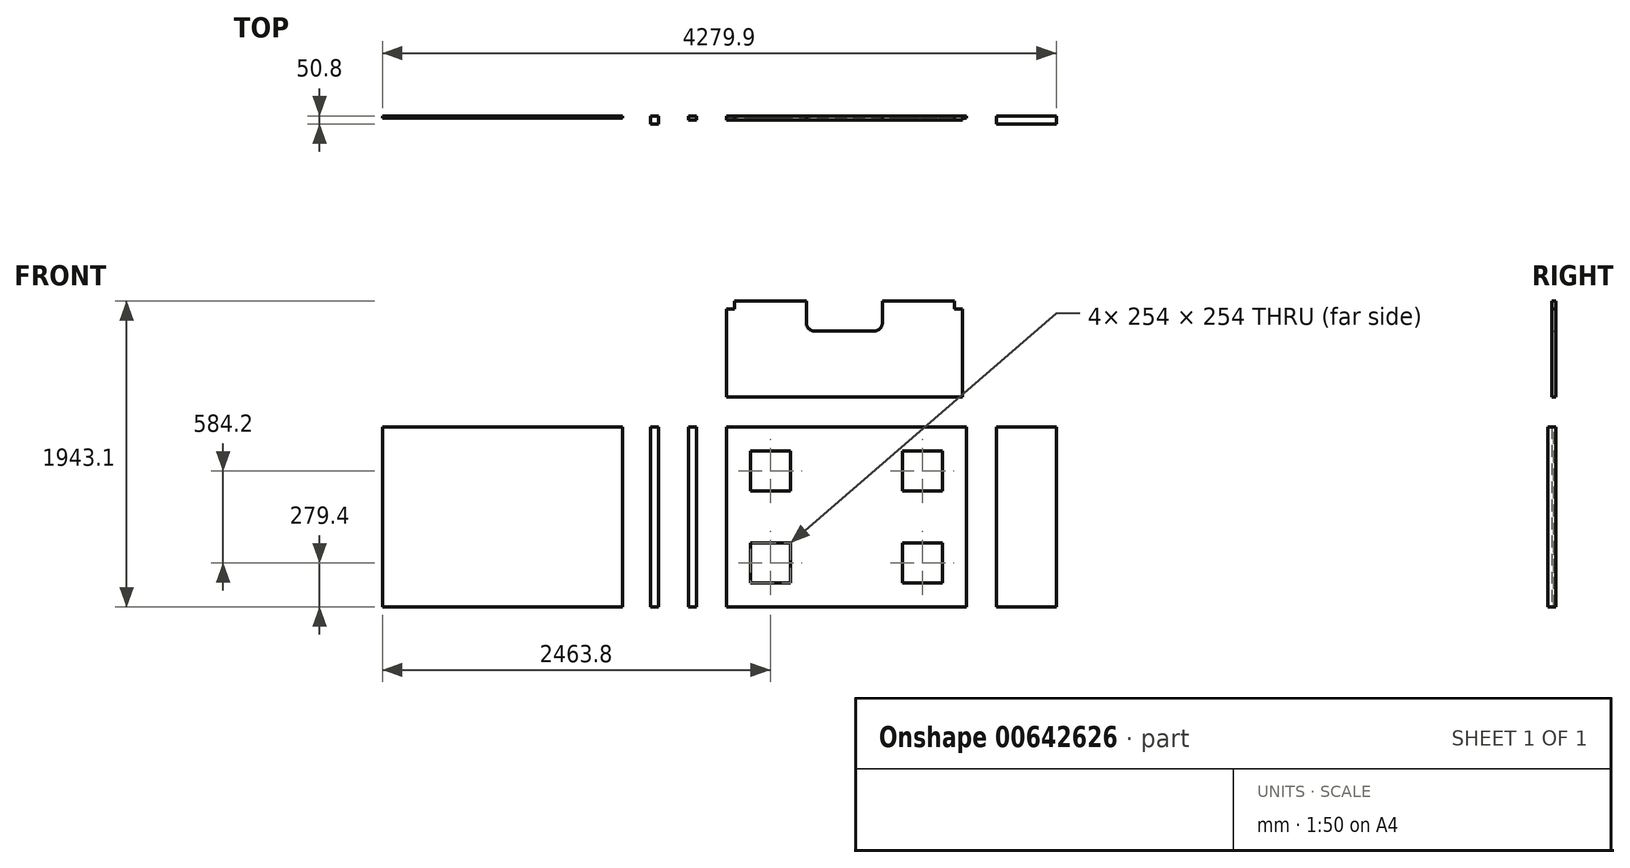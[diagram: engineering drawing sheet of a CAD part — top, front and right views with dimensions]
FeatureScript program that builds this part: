
annotation { "Feature Type Name" : "Feature", "Feature Type Description" : "" }
export const myFeature = defineFeature(function(context is Context, id is Id, definition is map)
    precondition{}
    {
        {
            var Q0;
            Q0=qCreatedBy(makeId("Front.planeOp"),FACE);
            var sketch = newSketch(context, id + "F0", { "sketchPlane" : qUnion([Q0])});
            skLineSegment(sketch, "E0.bottom", {"start": v(0, 1143) * mm, "end": v(50.8, 1143) * mm});
            skLineSegment(sketch, "E0.top", {"start": v(0, 0) * mm, "end": v(50.8, 0) * mm});
            skLineSegment(sketch, "E0.left", {"start": v(0, 1143) * mm, "end": v(0, 0) * mm});
            skLineSegment(sketch, "E0.right", {"start": v(50.8, 1143) * mm, "end": v(50.8, 0) * mm});
            skSolve(sketch);
        }
        {
            var Q0;
            Q0 = qSketchRegion(id + "F0", true);
            extrude(context, id + "F1", {"entities" : qUnion([Q0]), "depth" : 50.8 * mm, "offsetDistance" : 25.4 * mm});
        }
        {
            var Q0;
            Q0=qCreatedBy(makeId("Front.planeOp"),FACE);
            var sketch = newSketch(context, id + "F2", { "sketchPlane" : qUnion([Q0])});
            skLineSegment(sketch, "E1.bottom", {"start": v(241.3, 1143) * mm, "end": v(292.1, 1143) * mm});
            skLineSegment(sketch, "E1.top", {"start": v(241.3, 0) * mm, "end": v(292.1, 0) * mm});
            skLineSegment(sketch, "E1.left", {"start": v(241.3, 1143) * mm, "end": v(241.3, 0) * mm});
            skLineSegment(sketch, "E1.right", {"start": v(292.1, 1143) * mm, "end": v(292.1, 0) * mm});
            skSolve(sketch);
        }
        {
            var Q0;
            Q0 = qSketchRegion(id + "F2", true);
            extrude(context, id + "F3", {"entities" : qUnion([Q0]), "depth" : 25.4 * mm, "offsetDistance" : 25.4 * mm});
        }
        {
            var Q0;
            Q0=qCreatedBy(makeId("Front.planeOp"),FACE);
            var sketch = newSketch(context, id + "F4", { "sketchPlane" : qUnion([Q0])});
            skLineSegment(sketch, "E2.bottom", {"start": v(-177.8, 0) * mm, "end": v(-1701.8, 0) * mm});
            skLineSegment(sketch, "E2.top", {"start": v(-177.8, 1143) * mm, "end": v(-1701.8, 1143) * mm});
            skLineSegment(sketch, "E2.left", {"start": v(-177.8, 0) * mm, "end": v(-177.8, 1143) * mm});
            skLineSegment(sketch, "E2.right", {"start": v(-1701.8, 0) * mm, "end": v(-1701.8, 1143) * mm});
            skSolve(sketch);
        }
        {
            var Q0;
            Q0 = qSketchRegion(id + "F4", true);
            extrude(context, id + "F5", {"entities" : qUnion([Q0]), "depth" : 12.7 * mm, "offsetDistance" : 25.4 * mm});
        }
        {
            var Q0;
            Q0=qCreatedBy(makeId("Front.planeOp"),FACE);
            var sketch = newSketch(context, id + "F6", { "sketchPlane" : qUnion([Q0])});
            skLineSegment(sketch, "E3.bottom", {"start": v(482.6, 1143) * mm, "end": v(2006.6, 1143) * mm});
            skLineSegment(sketch, "E3.top", {"start": v(482.6, 0) * mm, "end": v(2006.6, 0) * mm});
            skLineSegment(sketch, "E3.left", {"start": v(482.6, 1143) * mm, "end": v(482.6, 0) * mm});
            skLineSegment(sketch, "E3.right", {"start": v(2006.6, 1143) * mm, "end": v(2006.6, 0) * mm});
            skLineSegment(sketch, "E4.bottom", {"start": v(635, 990.6) * mm, "end": v(889, 990.6) * mm});
            skLineSegment(sketch, "E4.top", {"start": v(635, 736.6) * mm, "end": v(889, 736.6) * mm});
            skLineSegment(sketch, "E4.left", {"start": v(635, 990.6) * mm, "end": v(635, 736.6) * mm});
            skLineSegment(sketch, "E4.right", {"start": v(889, 990.6) * mm, "end": v(889, 736.6) * mm});
            skLineSegment(sketch, "E5.bottom", {"start": v(635, 406.4) * mm, "end": v(889, 406.4) * mm});
            skLineSegment(sketch, "E5.top", {"start": v(635, 152.4) * mm, "end": v(889, 152.4) * mm});
            skLineSegment(sketch, "E5.left", {"start": v(635, 406.4) * mm, "end": v(635, 152.4) * mm});
            skLineSegment(sketch, "E5.right", {"start": v(889, 406.4) * mm, "end": v(889, 152.4) * mm});
            skLineSegment(sketch, "E6.bottom", {"start": v(1600.2, 990.6) * mm, "end": v(1854.2, 990.6) * mm});
            skLineSegment(sketch, "E6.top", {"start": v(1600.2, 736.6) * mm, "end": v(1854.2, 736.6) * mm});
            skLineSegment(sketch, "E6.left", {"start": v(1600.2, 990.6) * mm, "end": v(1600.2, 736.6) * mm});
            skLineSegment(sketch, "E6.right", {"start": v(1854.2, 990.6) * mm, "end": v(1854.2, 736.6) * mm});
            skLineSegment(sketch, "E7.bottom", {"start": v(1854.2, 406.4) * mm, "end": v(1600.2, 406.4) * mm});
            skLineSegment(sketch, "E7.top", {"start": v(1854.2, 152.4) * mm, "end": v(1600.2, 152.4) * mm});
            skLineSegment(sketch, "E7.left", {"start": v(1854.2, 406.4) * mm, "end": v(1854.2, 152.4) * mm});
            skLineSegment(sketch, "E7.right", {"start": v(1600.2, 406.4) * mm, "end": v(1600.2, 152.4) * mm});
            skLineSegment(sketch, "E8", {"start": v(1244.6, 1143) * mm, "end": v(1244.6, 0) * mm, "construction": true});
            skLineSegment(sketch, "E9", {"start": v(482.6, 571.5) * mm, "end": v(2006.6, 571.5) * mm, "construction": true});
            skSolve(sketch);
        }
        {
            var Q0;
            Q0 = qSketchRegion(id + "F6", true);
            extrude(context, id + "F7", {"entities" : qUnion([Q0]), "depth" : 12.7 * mm, "offsetDistance" : 25.4 * mm});
        }
        {
            var Q0;
            Q0=qCreatedBy(makeId("Front.planeOp"),FACE);
            var sketch = newSketch(context, id + "F8", { "sketchPlane" : qUnion([Q0])});
            skLineSegment(sketch, "E10.bottom", {"start": v(482.6, 1333.5) * mm, "end": v(1981.2, 1333.5) * mm});
            skLineSegment(sketch, "E11.top", {"start": v(1041.4, 1752.6) * mm, "end": v(1422.4, 1752.6) * mm});
            skLineSegment(sketch, "E11.left", {"start": v(990.6, 1943.1) * mm, "end": v(990.6, 1803.4) * mm});
            skLineSegment(sketch, "E11.right", {"start": v(1473.2, 1943.1) * mm, "end": v(1473.2, 1803.4) * mm});
            skPoint(sketch, "E12.visualSharp", {"position": v(990.6, 1752.6) * mm});
            skArc(sketch, "E12.filletArc", {"start": v(990.6, 1803.4) * mm, "mid": v(1005.48, 1767.48) * mm, "end": v(1041.4, 1752.6) * mm});
            skPoint(sketch, "E13.visualSharp", {"position": v(1473.2, 1752.6) * mm});
            skArc(sketch, "E13.filletArc", {"start": v(1422.4, 1752.6) * mm, "mid": v(1458.32, 1767.48) * mm, "end": v(1473.2, 1803.4) * mm});
            skLineSegment(sketch, "E14", {"start": v(482.6, 1892.3) * mm, "end": v(533.4, 1892.3) * mm});
            skLineSegment(sketch, "E15", {"start": v(533.4, 1892.3) * mm, "end": v(533.4, 1943.1) * mm});
            skLineSegment(sketch, "E16", {"start": v(1930.4, 1943.1) * mm, "end": v(1930.4, 1892.3) * mm});
            skLineSegment(sketch, "E17", {"start": v(1930.4, 1892.3) * mm, "end": v(1981.2, 1892.3) * mm});
            skLineSegment(sketch, "E18", {"start": v(533.4, 1943.1) * mm, "end": v(990.6, 1943.1) * mm});
            skLineSegment(sketch, "E19", {"start": v(1473.2, 1943.1) * mm, "end": v(1930.4, 1943.1) * mm});
            skLineSegment(sketch, "E20", {"start": v(482.6, 1892.3) * mm, "end": v(482.6, 1333.5) * mm});
            skLineSegment(sketch, "E21", {"start": v(1981.2, 1333.5) * mm, "end": v(1981.2, 1892.3) * mm});
            skSolve(sketch);
        }
        {
            var Q0;
            Q0 = qSketchRegion(id + "F8", true);
            extrude(context, id + "F9", {"entities" : qUnion([Q0]), "depth" : 25.4 * mm, "offsetDistance" : 25.4 * mm});
        }
        {
            var Q0;
            Q0=qCreatedBy(makeId("Front.planeOp"),FACE);
            var sketch = newSketch(context, id + "F10", { "sketchPlane" : qUnion([Q0])});
            skLineSegment(sketch, "E22.bottom", {"start": v(2197.1, 0) * mm, "end": v(2578.1, 0) * mm});
            skLineSegment(sketch, "E22.top", {"start": v(2197.1, 1143) * mm, "end": v(2578.1, 1143) * mm});
            skLineSegment(sketch, "E22.left", {"start": v(2197.1, 0) * mm, "end": v(2197.1, 1143) * mm});
            skLineSegment(sketch, "E22.right", {"start": v(2578.1, 0) * mm, "end": v(2578.1, 1143) * mm});
            skSolve(sketch);
        }
        {
            var Q0;
            Q0 = qSketchRegion(id + "F10", true);
            extrude(context, id + "F11", {"entities" : qUnion([Q0]), "depth" : 50.8 * mm, "offsetDistance" : 25.4 * mm});
        }
    });
